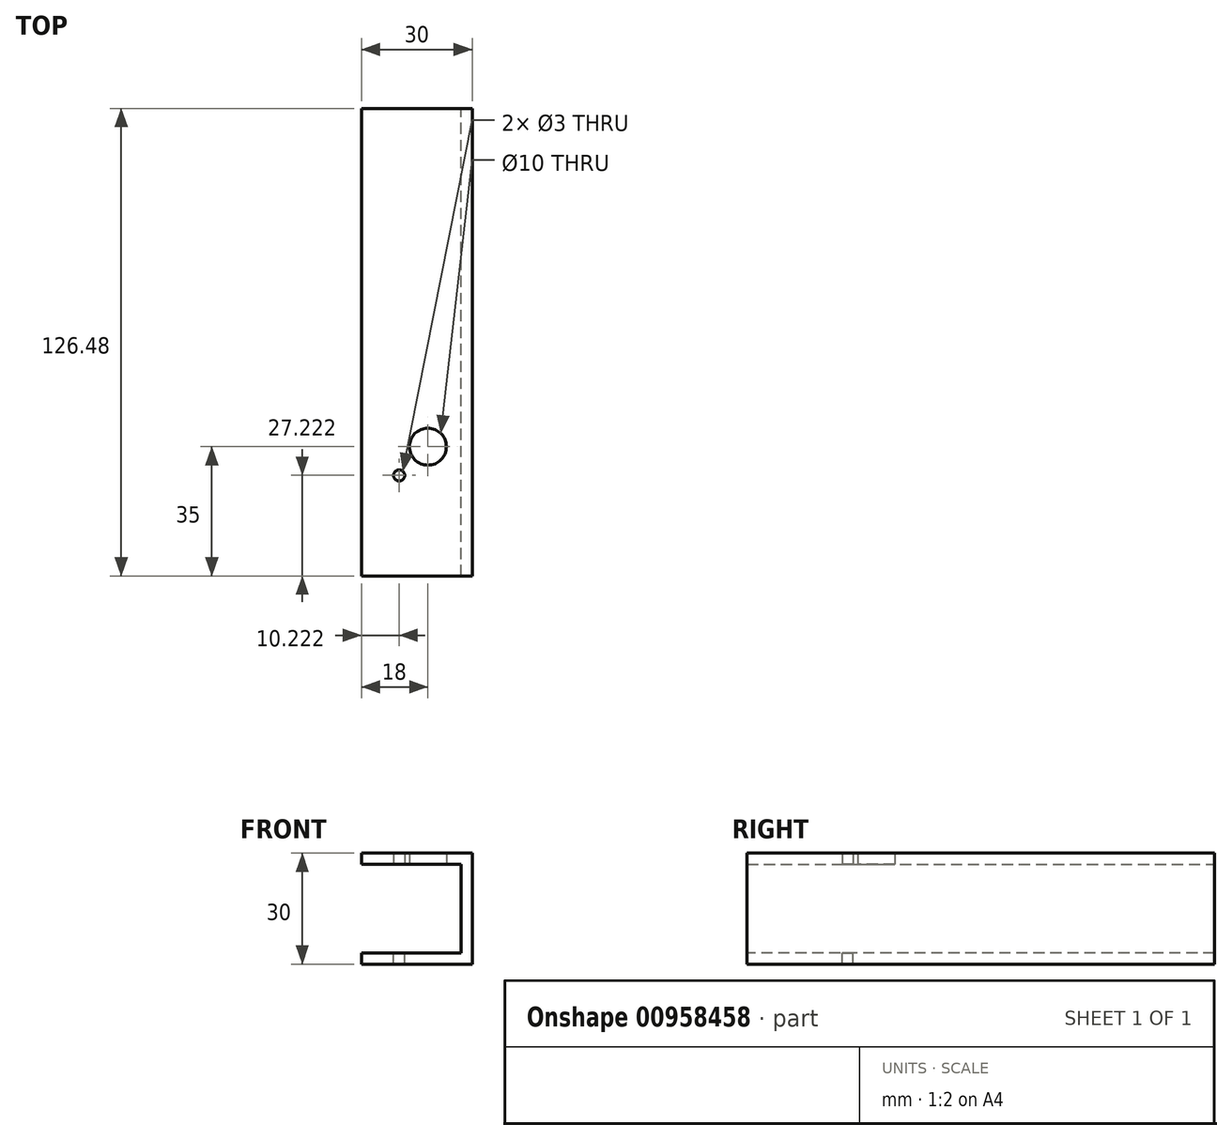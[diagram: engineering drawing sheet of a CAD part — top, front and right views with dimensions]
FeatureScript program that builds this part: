
annotation { "Feature Type Name" : "Feature", "Feature Type Description" : "" }
export const myFeature = defineFeature(function(context is Context, id is Id, definition is map)
    precondition{}
    {
        {
            var Q0;
            Q0=qCreatedBy(makeId("Top.planeOp"),FACE);
            var sketch = newSketch(context, id + "F0", { "sketchPlane" : qUnion([Q0])});
            skArc(sketch, "E0", {"start": v(0, 7.65) * mm, "mid": v(-6.12, 4.6) * mm, "end": v(-7.34, -2.14) * mm});
            skLineSegment(sketch, "E1", {"start": v(0, 7.65) * mm, "end": v(11.35, 7.65) * mm});
            skLineSegment(sketch, "E2", {"start": v(11.35, 7.65) * mm, "end": v(11.35, -7.65) * mm, "construction": true});
            skLineSegment(sketch, "E3", {"start": v(11.35, -7.65) * mm, "end": v(0, -7.65) * mm});
            skLineSegment(sketch, "E4", {"start": v(-7.78, -7.78) * mm, "end": v(-31.7, -31.7) * mm, "construction": true});
            skCircle(sketch, "E5", {"center": v(0, 0) * mm, "radius": 5 * mm});
            skLineSegment(sketch, "E6.trimOffspring", {"start": v(-7.34, -2.14) * mm, "end": v(-7.34, -2.14) * mm});
            skLineSegment(sketch, "E7", {"start": v(12, -35) * mm, "end": v(12, 91.48) * mm});
            skLineSegment(sketch, "E8", {"start": v(12, 91.48) * mm, "end": v(-18, 91.48) * mm});
            skLineSegment(sketch, "E9", {"start": v(-18, 91.48) * mm, "end": v(-18, -35) * mm});
            skLineSegment(sketch, "E10", {"start": v(-18, -35) * mm, "end": v(12, -35) * mm});
            skCircle(sketch, "E11", {"center": v(0, 0) * mm, "radius": 8 * mm, "construction": true});
            skLineSegment(sketch, "E12.MirrorCS", {"start": v(-7.34, -2.14) * mm, "end": v(-9.99, -6.4) * mm});
            skArc(sketch, "E13.MirrorCS", {"start": v(-9.99, -6.4) * mm, "mid": v(-9.62, -9.62) * mm, "end": v(-6.4, -9.99) * mm});
            skLineSegment(sketch, "E14.MirrorCS", {"start": v(-2.14, -7.34) * mm, "end": v(-6.4, -9.99) * mm});
            skCircle(sketch, "E15.MirrorC", {"center": v(-7.78, -7.78) * mm, "radius": 1.5 * mm});
            skLineSegment(sketch, "E16", {"start": v(-7.34, 2.14) * mm, "end": v(-7.34, 2.14) * mm});
            skArc(sketch, "E17.trimOffspring", {"start": v(-2.14, -7.34) * mm, "mid": v(-1.08, -7.57) * mm, "end": v(0, -7.65) * mm});
            skLineSegment(sketch, "E18", {"start": v(-7.78, -7.78) * mm, "end": v(0, 0) * mm});
            skSolve(sketch);
        }
        {
            var Q0;
            Q0 = qSketchRegion(id + "F0", true);
            extrude(context, id + "F1", {"entities" : qUnion([Q0]), "depth" : 3 * mm, "offsetDistance" : 25 * mm});
        }
        {
            var Q0;
            Q0=makeQuery(id+"F1.opExtrude","CAP_FACE",FACE,{"disambiguationData":[OSD([sQuery(id+"F0.wireOp",EDGE,"DuqUoLTQ-mZma-7YvE-XBHo-BAhsoqr58RGC"),sQuery(id+"F0.wireOp",EDGE,"E5"),sQuery(id+"F0.wireOp",EDGE,"E7"),sQuery(id+"F0.wireOp",EDGE,"E8"),sQuery(id+"F0.wireOp",EDGE,"E9"),sQuery(id+"F0.wireOp",EDGE,"E10")])],"isStart":false});
            var sketch = newSketch(context, id + "F2", { "sketchPlane" : qUnion([Q0])});
            skLineSegment(sketch, "E19.0", {"start": v(12, -35) * mm, "end": v(12, 91.48) * mm});
            skLineSegment(sketch, "E20", {"start": v(12, -35) * mm, "end": v(9, -35) * mm});
            skLineSegment(sketch, "E21", {"start": v(9, -35) * mm, "end": v(9, 91.48) * mm});
            skLineSegment(sketch, "E22", {"start": v(9, 91.48) * mm, "end": v(12, 91.48) * mm});
            skSolve(sketch);
        }
        {
            var Q0;
            Q0 = qSketchRegion(id + "F2", true);
            extrude(context, id + "F3", {"entities" : qUnion([Q0]), "operationType" : NewBodyOperationType.ADD, "oppositeDirection" : true, "depth" : 30 * mm, "offsetDistance" : 25 * mm});
        }
        {
            var Q0;
            Q0 = qSketchRegion(id + "F0", true);
            var Q1;
            Q1=makeQuery(id+"F0.imprint","IMPRINT",FACE,{"disambiguationData":[TD([[makeQuery(id+"F0.imprint","IMPRINT",EDGE,{"derivedFrom":sQuery(id+"F0.wireOp",EDGE,"E5")}),1.0]])]});
            var Q2;
            Q2=makeQuery(id+"F0.imprint","IMPRINT",FACE,{"disambiguationData":[TD([[makeQuery(id+"F0.imprint","IMPRINT",EDGE,{"derivedFrom":sQuery(id+"F0.wireOp",EDGE,"E15.MirrorC")}),-1.0]])]});
            extrude(context, id + "F4", {"entities" : qUnion([Q0, Q1, Q2]), "operationType" : NewBodyOperationType.ADD, "oppositeDirection" : true, "depth" : 27 * mm, "offsetDistance" : 25 * mm, "hasSecondDirection" : true, "secondDirectionOppositeDirection" : true, "secondDirectionDepth" : 24 * mm});
        }
    });
